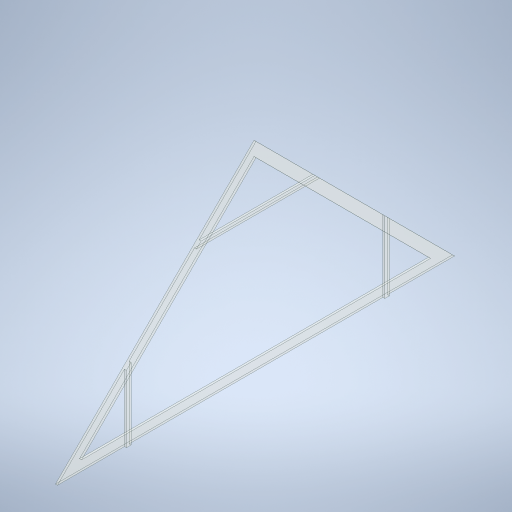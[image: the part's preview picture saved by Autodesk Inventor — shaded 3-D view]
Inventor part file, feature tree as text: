
AUTODESK INVENTOR PART (.ipt)
format: ipt  version: 2024 (Build 280153000, 153)  size: 289,792 bytes
history: native  units: in
note: dims shown in document units (in); Inventor stores cm internally (conversion verified against a paired STEP export)
features: extrude x2, sketch x2
ambient origin geometry x8: Origin, YZ Plane, XZ Plane, XY Plane, X Axis, Y Axis, Z Axis, Center Point
bodies: Solid1 (feature_tree)
feature tree (4):
  extrude  "Extrusion1"  Depth=1.5in TaperAngle=0.0deg
  extrude  "Extrusion2"  Depth=7.5in
  sketch  "Sketch1"  dims[d2=45.0deg d3=1.5in d4=0.0in]
  sketch  "Sketch2"  dims[d5=300.0in d6=7.5in d7=3.5in d9=96.0in d10=3.5in d11=36.0in d12=3.5in d14=36.0in d15=1.5in d16=0.0in]
